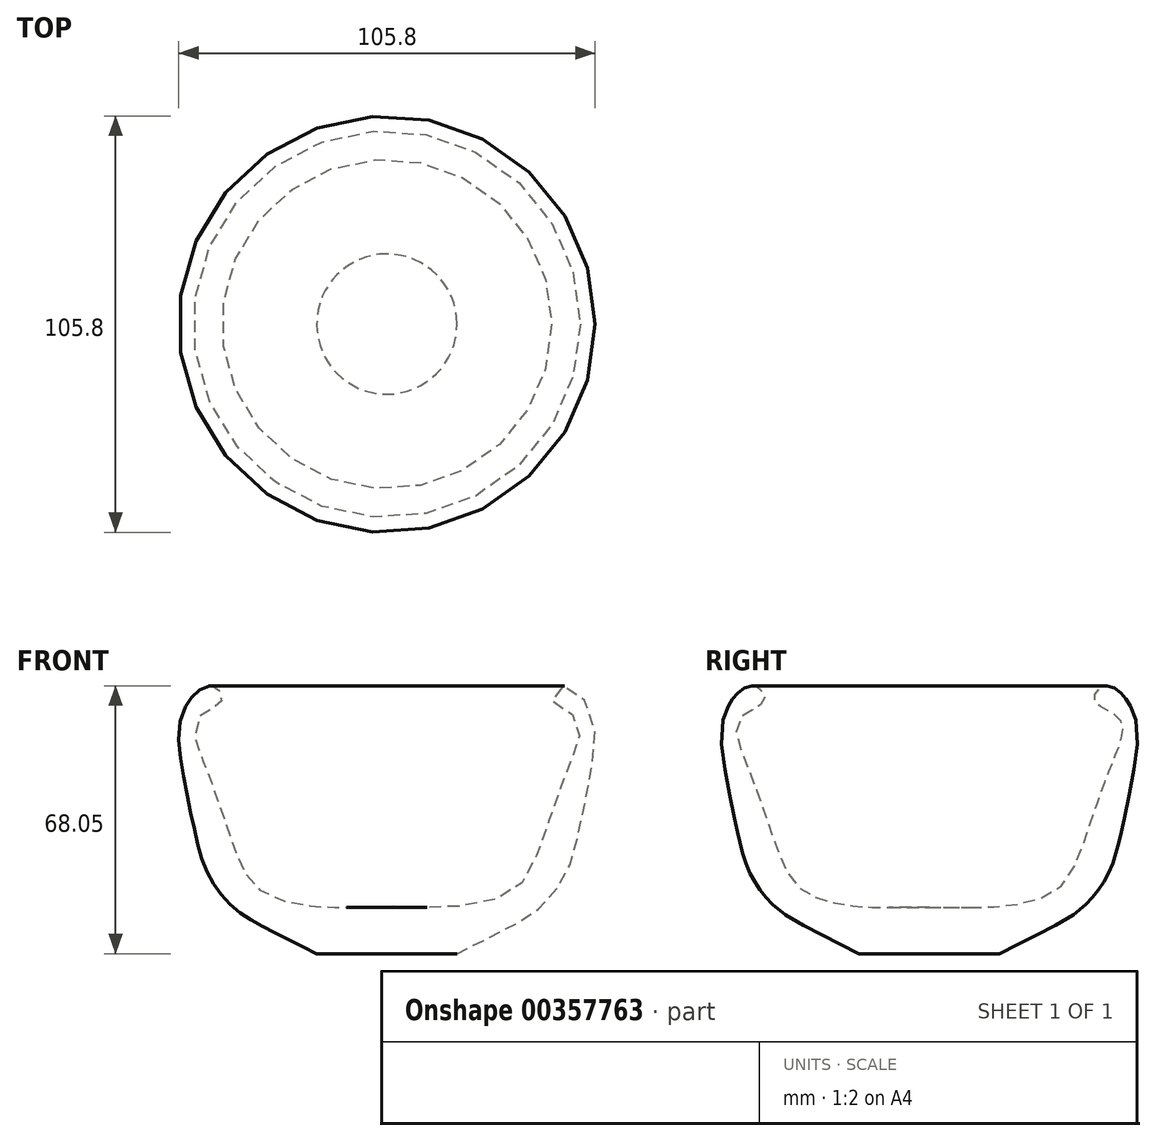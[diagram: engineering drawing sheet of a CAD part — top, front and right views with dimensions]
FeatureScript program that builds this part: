
annotation { "Feature Type Name" : "Feature", "Feature Type Description" : "" }
export const myFeature = defineFeature(function(context is Context, id is Id, definition is map)
    precondition{}
    {
        {
            var Q0;
            Q0=qCreatedBy(makeId("Front.planeOp"),FACE);
            var sketch = newSketch(context, id + "F0", { "sketchPlane" : qUnion([Q0])});
            skLineSegment(sketch, "E0", {"start": v(0, 0) * mm, "end": v(0, 12) * mm});
            skLineSegment(sketch, "E1", {"start": v(0, 0) * mm, "end": v(17.82, 0) * mm});
            skFitSpline(sketch, "E2", {"points": [v(17.82, 0) * mm, v(31.57, 6.96) * mm, v(39.29, 12) * mm, v(45.33, 20.04) * mm, v(48.35, 29.1) * mm, v(52.04, 47.22) * mm, v(51.7, 61.64) * mm, v(44.66, 68.02) * mm, v(41.97, 64.33) * mm, v(48.35, 59.63) * mm, v(48.01, 52.25) * mm, v(45, 44.53) * mm, v(38.95, 27.43) * mm, v(32.58, 16.35) * mm, v(17.82, 12) * mm, v(0, 12) * mm], "startDerivative": vector(191.49, 95.47) * mm, "endDerivative": vector(-213.93, 9.26) * mm});
            skSolve(sketch);
        }
        {
            var Q0;
            Q0=sQuery(id+"F0.wireOp",EDGE,"E2");
            var Q1;
            Q1=sQuery(id+"F0.wireOp",EDGE,"E0");
            revolve(context, id + "F1", {"bodyType" : ToolBodyType.SURFACE, "surfaceEntities" : qUnion([Q0]), "axis" : qUnion([Q1]), "revolveType" : RevolveType.FULL});
        }
    });
